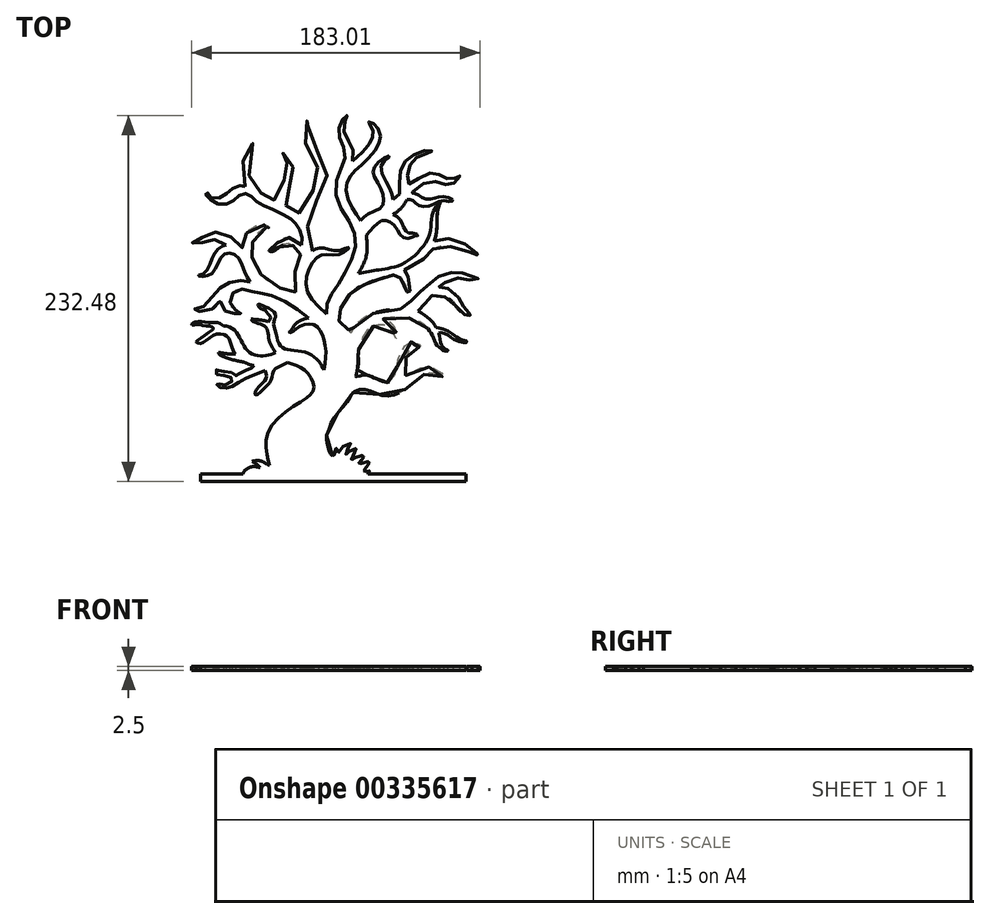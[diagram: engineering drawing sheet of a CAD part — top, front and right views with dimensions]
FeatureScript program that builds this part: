
annotation { "Feature Type Name" : "Feature", "Feature Type Description" : "" }
export const myFeature = defineFeature(function(context is Context, id is Id, definition is map)
    precondition{}
    {
        {
            var Q0;
            Q0=qCreatedBy(makeId("Top.planeOp"),FACE);
            var sketch = newSketch(context, id + "F0", { "sketchPlane" : qUnion([Q0])});
            skFitSpline(sketch, "E0", {"points": [v(-37.23, -92.22) * mm, v(-37.93, -89.5) * mm, v(-37.64, -70.07) * mm, v(-14, -49.38) * mm, v(-9.05, -42.86) * mm, v(-12.92, -33.47) * mm, v(-20.4, -28.62) * mm, v(-30.52, -26.33) * mm, v(-44.65, -28.9) * mm, v(-53.5, -26.46) * mm], "startDerivative": vector(-6.46, 28.02) * mm, "endDerivative": vector(-86.12, 39.68) * mm});
            skFitSpline(sketch, "E1", {"points": [v(-53.5, -26.46) * mm, v(-62.24, -24.53) * mm, v(-69.12, -21.43) * mm, v(-69.55, -20.32) * mm], "startDerivative": vector(-17.56, 2.77) * mm, "endDerivative": vector(-0.49, 6.57) * mm});
            skFitSpline(sketch, "E2", {"points": [v(-69.55, -20.32) * mm, v(-63.18, -21.35) * mm, v(-58.8, -21.52) * mm], "startDerivative": vector(12.15, -2.3) * mm, "endDerivative": vector(9.28, -0.04) * mm});
            skFitSpline(sketch, "E3", {"points": [v(-58.8, -21.52) * mm, v(-61.03, -17.47) * mm, v(-63.61, -10.67) * mm, v(-71.93, -9.08) * mm, v(-80.86, -14.69) * mm, v(-83.78, -13.74) * mm, v(-82.12, -12.32) * mm, v(-68.6, -3.79) * mm, v(-58.2, -7.58) * mm, v(-51.73, -18.6) * mm, v(-42.1, -22.64) * mm, v(-33.23, -20.57) * mm], "startDerivative": vector(-32.51, 46.9) * mm, "endDerivative": vector(77.44, 28.59) * mm});
            skFitSpline(sketch, "E4", {"points": [v(-33.23, -20.57) * mm, v(-37.27, -13.17) * mm, v(-39.86, -4.05) * mm, v(-47.76, -0.64) * mm, v(-48.83, 0.83) * mm], "startDerivative": vector(-16.8, 23.88) * mm, "endDerivative": vector(0.64, 6.3) * mm});
            skFitSpline(sketch, "E5", {"points": [v(-48.83, 0.83) * mm, v(-35.48, -2.55) * mm, v(-31.57, -14.02) * mm, v(-26.34, -18.5) * mm, v(-14.47, -20.28) * mm, v(-5.83, -26.09) * mm, v(-2.67, -31.48) * mm], "startDerivative": vector(73.32, -8.54) * mm, "endDerivative": vector(18.96, -39.09) * mm});
            skFitSpline(sketch, "E6", {"points": [v(-2.67, -31.48) * mm, v(-1.43, -19.6) * mm, v(-3.36, -10.05) * mm, v(-7.1, -3.92) * mm, v(-12.97, -2.37) * mm, v(-19.74, -4.89) * mm, v(-22.7, -7.34) * mm, v(-24.45, -7.73) * mm, v(-24.64, -7.2) * mm, v(-23.41, -6.37) * mm, v(-21.54, -3.28) * mm, v(-17.68, 0) * mm, v(-12.52, 1.37) * mm], "startDerivative": vector(16.4, 90.94) * mm, "endDerivative": vector(60.2, 10.33) * mm});
            skFitSpline(sketch, "E7", {"points": [v(-12.52, 1.37) * mm, v(-24.06, 10) * mm, v(-38, 16.41) * mm, v(-45.65, 17.78) * mm, v(-49.75, 18.87) * mm, v(-57.81, 19.42) * mm, v(-62.18, 13.68) * mm, v(-60.95, 8.35) * mm, v(-56.05, 5.43) * mm, v(-55.53, 4.23) * mm, v(-58.2, 4.23) * mm, v(-64.66, 5.34) * mm, v(-68.36, 11.89) * mm, v(-68.7, 12.49) * mm, v(-69.22, 12.32) * mm, v(-70.43, 10) * mm, v(-78.6, 5.6) * mm, v(-84.97, 6.9) * mm, v(-84.8, 7.24) * mm, v(-79.3, 8.79) * mm, v(-71.63, 17.4) * mm, v(-65, 22.99) * mm, v(-55.7, 25.14) * mm, v(-49.5, 24.45) * mm], "startDerivative": vector(-156.26, 128.1) * mm, "endDerivative": vector(126.07, -24.69) * mm});
            skFitSpline(sketch, "E8", {"points": [v(-49.5, 24.45) * mm, v(-52.85, 30.29) * mm, v(-56.83, 39.4) * mm, v(-61.9, 42.67) * mm, v(-66.9, 41.22) * mm, v(-70.51, 35) * mm, v(-73.99, 29.64) * mm, v(-78.7, 28.05) * mm, v(-82.24, 28.19) * mm, v(-82.31, 28.62) * mm, v(-81.95, 28.7) * mm, v(-78.9, 29.64) * mm, v(-74.78, 36.15) * mm, v(-72.25, 42.38) * mm, v(-67.83, 46.86) * mm, v(-64.72, 47.95) * mm], "startDerivative": vector(-43.88, 65.41) * mm, "endDerivative": vector(53.78, 11.6) * mm});
            skFitSpline(sketch, "E9", {"points": [v(-64.72, 47.95) * mm, v(-68.7, 50.12) * mm, v(-73.4, 51.28) * mm, v(-78.33, 50.27) * mm, v(-80.5, 49.18) * mm, v(-85.35, 48.96) * mm, v(-86.07, 49.1) * mm, v(-85.78, 49.61) * mm, v(-82.89, 50.92) * mm, v(-78.62, 53.81) * mm, v(-72.9, 55.91) * mm, v(-65.52, 54.75) * mm, v(-59.37, 50.84) * mm, v(-54.73, 46.28) * mm, v(-54.3, 46.5) * mm, v(-52.49, 53.96) * mm, v(-44.31, 60.4) * mm, v(-37.43, 59.68) * mm, v(-37.65, 59.1) * mm, v(-38.8, 59.24) * mm, v(-46.4, 53.02) * mm, v(-48.65, 44.48) * mm, v(-47.93, 38.47) * mm, v(-42.28, 28.99) * mm, v(-29.9, 20.37) * mm, v(-20.79, 17.84) * mm, v(-20.71, 18.06) * mm, v(-21.3, 28.26) * mm, v(-18.04, 39.84) * mm, v(-17.75, 42.6) * mm, v(-19.77, 45.63) * mm, v(-25.27, 48.67) * mm, v(-30.85, 46.65) * mm, v(-35.26, 43.75) * mm, v(-37.43, 44.19) * mm, v(-37.22, 44.55) * mm, v(-35.77, 45.34) * mm, v(-31.43, 50.34) * mm, v(-27.23, 52.58) * mm, v(-21.44, 51.71) * mm, v(-16.73, 47.95) * mm], "startDerivative": vector(-159.85, 95.28) * mm, "endDerivative": vector(153.51, -155.1) * mm});
            skFitSpline(sketch, "E10", {"points": [v(-16.73, 47.95) * mm, v(-16.73, 53.67) * mm, v(-19.41, 59.82) * mm, v(-21.8, 62.93) * mm, v(-27.3, 66.7) * mm, v(-38.3, 71.84) * mm, v(-45.4, 75.53) * mm, v(-48.58, 78.71) * mm, v(-52.78, 80.67) * mm, v(-57.48, 78.57) * mm, v(-61.97, 74.88) * mm, v(-68.63, 73.57) * mm, v(-75.36, 77.2) * mm, v(-77.68, 80.45) * mm, v(-76.66, 81.24) * mm, v(-76.45, 80.23) * mm, v(-72.76, 77.34) * mm, v(-65.37, 79.87) * mm, v(-60.52, 83.78) * mm, v(-54.95, 85.59) * mm, v(-52.63, 85.08) * mm], "startDerivative": vector(12.24, 106.84) * mm, "endDerivative": vector(59.66, -23.4) * mm});
            skFitSpline(sketch, "E11", {"points": [v(-52.63, 85.08) * mm, v(-54.59, 91.38) * mm, v(-53.72, 102.23) * mm, v(-50.25, 108.9) * mm, v(-47.86, 112) * mm, v(-47.86, 112.8) * mm, v(-47.5, 113.45) * mm, v(-46.63, 113.02) * mm, v(-46.77, 111.14) * mm, v(-47.93, 109.11) * mm, v(-50.25, 102.3) * mm, v(-50.17, 92.1) * mm, v(-47.06, 85.66) * mm, v(-42.72, 81.24) * mm, v(-41.78, 79.8) * mm, v(-35.77, 76.25) * mm, v(-34.32, 75.82) * mm, v(-34.25, 76.76) * mm, v(-31.79, 83.42) * mm, v(-28.17, 88.34) * mm, v(-25.27, 93.33) * mm, v(-25.2, 98.1) * mm, v(-27.23, 101.87) * mm, v(-29.11, 103.9) * mm, v(-29.62, 105.78) * mm, v(-29.26, 106.43) * mm, v(-28.53, 105.85) * mm, v(-28.82, 104.91) * mm, v(-26.72, 103.25) * mm, v(-22.16, 96.73) * mm, v(-21.94, 90) * mm, v(-24.7, 83.92) * mm, v(-27.37, 78.35) * mm, v(-27.37, 74.15) * mm, v(-26.65, 72.63) * mm, v(-22.81, 70.39) * mm, v(-18.76, 67.28) * mm, v(-18.69, 67.64) * mm, v(-12.97, 78.06) * mm, v(-9.93, 81.9) * mm, v(-6.38, 90) * mm, v(-6.31, 96.52) * mm, v(-11.09, 106) * mm, v(-14.63, 113.53) * mm, v(-15.5, 119.39) * mm, v(-13.4, 126.92) * mm, v(-11.81, 128.94) * mm, v(-11.23, 128.3) * mm, v(-11.74, 127.57) * mm, v(-12.82, 122) * mm, v(-10.44, 113.67) * mm, v(-5.3, 105.5) * mm, v(-1.03, 98.04) * mm, v(-1.53, 85.73) * mm, v(-5.95, 77.84) * mm, v(-12.32, 68.8) * mm, v(-12.82, 59.39) * mm, v(-10.87, 56.42) * mm, v(-9.93, 44.19) * mm], "startDerivative": vector(-120.08, 280.65) * mm, "endDerivative": vector(-5.28, -540.47) * mm});
            skFitSpline(sketch, "E12", {"points": [v(-9.93, 44.19) * mm, v(-7.69, 45.56) * mm, v(-3.85, 46.07) * mm, v(1.36, 44.9) * mm, v(7, 44.19) * mm, v(12.36, 46.21) * mm, v(13.3, 46.14) * mm, v(11.57, 44.19) * mm, v(5.7, 41.5) * mm, v(-2.26, 41.8) * mm, v(-7.18, 39.77) * mm, v(-12.68, 31.01) * mm, v(-13.26, 18.64) * mm, v(-1.03, 4.16) * mm], "startDerivative": vector(40.45, 30.37) * mm, "endDerivative": vector(114.16, -103.83) * mm});
            skFitSpline(sketch, "E13", {"points": [v(-1.03, 4.16) * mm, v(0, 12.2) * mm, v(5.27, 20.94) * mm, v(12.32, 33.52) * mm, v(17.54, 48.24) * mm, v(14.16, 61.43) * mm, v(5.88, 76.46) * mm, v(6.19, 92.1) * mm, v(10.8, 102.53) * mm, v(9.1, 112.04) * mm, v(6.65, 119.25) * mm, v(8.34, 126.15) * mm, v(10.94, 129.83) * mm, v(12.17, 129.99) * mm, v(10.8, 126.15) * mm, v(10.94, 117.72) * mm, v(15.24, 110.2) * mm, v(15.54, 101.3) * mm], "startDerivative": vector(2.52, 146.68) * mm, "endDerivative": vector(-17.17, -159.84) * mm});
            skFitSpline(sketch, "E14", {"points": [v(15.54, 101.3) * mm, v(20.45, 105.45) * mm, v(23.52, 108.67) * mm, v(27.05, 113.73) * mm, v(28.43, 120.94) * mm, v(25.97, 125.08) * mm, v(25.97, 126) * mm, v(29.8, 124.31) * mm, v(33.18, 117.1) * mm, v(29.96, 108.05) * mm, v(20, 97.62) * mm, v(13.86, 91.18) * mm, v(11.25, 83.36) * mm, v(15.54, 71.25) * mm, v(20.76, 63.27) * mm], "startDerivative": vector(77.02, 62.47) * mm, "endDerivative": vector(65.04, -83.73) * mm});
            skFitSpline(sketch, "E15", {"points": [v(20.76, 63.27) * mm, v(25.05, 67.26) * mm, v(33.95, 71.86) * mm, v(35.33, 76.61) * mm, v(33.34, 84.44) * mm, v(28.58, 93.33) * mm, v(31.19, 99.47) * mm, v(38.24, 104.37) * mm, v(39.01, 103.91) * mm, v(33.8, 98.85) * mm, v(38.86, 84.44) * mm, v(41.16, 76.61) * mm], "startDerivative": vector(41.17, 51.56) * mm, "endDerivative": vector(11.33, -71.84) * mm});
            skFitSpline(sketch, "E16", {"points": [v(41.16, 76.61) * mm, v(45.45, 80.6) * mm, v(45.29, 90.93) * mm, v(48.66, 100.29) * mm, v(54.18, 105.04) * mm, v(63.67, 108.12) * mm, v(65.97, 107.5) * mm, v(65.66, 107.04) * mm, v(59.09, 104.9) * mm, v(52.95, 99.98) * mm, v(50.5, 92.31) * mm, v(51.6, 86.62) * mm, v(60.83, 92.2) * mm, v(68.8, 93.27) * mm, v(74.16, 90.66) * mm, v(79.38, 89.9) * mm, v(83.36, 92.2) * mm, v(83.67, 91.89) * mm, v(79.68, 86.98) * mm, v(73.7, 86.37) * mm, v(64.96, 88.51) * mm, v(53.89, 81.83) * mm, v(50.2, 76.61) * mm, v(45.76, 70.63) * mm, v(41.16, 67.26) * mm], "startDerivative": vector(110.78, 80.65) * mm, "endDerivative": vector(-110.46, -69.26) * mm});
            skFitSpline(sketch, "E17", {"points": [v(41.16, 67.26) * mm, v(45.24, 64.63) * mm, v(47.07, 61.26) * mm, v(49.26, 57.16) * mm, v(51.45, 55.51) * mm, v(55.55, 55.33) * mm, v(57, 53.78) * mm, v(56.37, 53.6) * mm, v(55.28, 53.7) * mm, v(50.9, 52.05) * mm, v(46.89, 53.33) * mm, v(42.96, 59.07) * mm, v(38.4, 63.08) * mm, v(34.03, 63.27) * mm, v(28.92, 59.25) * mm, v(24.36, 54.06) * mm], "startDerivative": vector(63.37, -31.9) * mm, "endDerivative": vector(-49.93, -59.23) * mm});
            skFitSpline(sketch, "E18", {"points": [v(24.36, 54.06) * mm, v(24.36, 41.38) * mm, v(19.25, 29.8) * mm], "startDerivative": vector(2.56, -25.89) * mm, "endDerivative": vector(-12.77, -22.63) * mm});
            skFitSpline(sketch, "E19", {"points": [v(19.25, 29.8) * mm, v(27.1, 31.26) * mm, v(35.21, 32.53) * mm, v(48.07, 36.27) * mm, v(61.84, 49.13) * mm, v(65.3, 59.07) * mm, v(66.22, 67.19) * mm, v(70.78, 74.76) * mm, v(71.14, 74.76) * mm, v(69.96, 71.47) * mm, v(69.14, 61.17) * mm, v(68.68, 54.97) * mm, v(67.5, 50.32) * mm], "startDerivative": vector(92.84, 17.97) * mm, "endDerivative": vector(-20.5, -69.36) * mm});
            skFitSpline(sketch, "E20", {"points": [v(67.5, 50.32) * mm, v(73.24, 51.87) * mm, v(83.73, 50.32) * mm, v(89.93, 45.85) * mm, v(95.13, 42.66) * mm, v(96.22, 42.38) * mm, v(96.22, 41.65) * mm, v(94.76, 41.56) * mm, v(94.58, 40.92) * mm, v(93.21, 41.47) * mm, v(84.73, 45.4) * mm, v(71.05, 46.76) * mm, v(64.94, 44.02) * mm, v(60.66, 38.92) * mm, v(48.17, 31.66) * mm, v(47.97, 31.21) * mm, v(49.1, 30.12) * mm, v(51.78, 24.65) * mm, v(52.02, 18.07) * mm, v(51.94, 16.29) * mm, v(50.88, 16.45) * mm, v(49.18, 23.11) * mm, v(44.38, 27.82) * mm, v(42.27, 28.31) * mm, v(41.78, 28.72) * mm, v(39.35, 28.15) * mm, v(28.54, 24.98) * mm, v(21.96, 22.14) * mm, v(13.75, 16.53) * mm, v(8.47, 8.57) * mm, v(6.93, 3.45) * mm, v(7.25, -1.34) * mm, v(12.21, -5.16) * mm, v(14.4, -7.84) * mm, v(14.9, -7.36) * mm, v(22.37, 1.34) * mm, v(46.09, 7.27) * mm], "startDerivative": vector(168, 66.2) * mm, "endDerivative": vector(398.56, 17.42) * mm});
            skFitSpline(sketch, "E21", {"points": [v(46.09, 7.27) * mm, v(52.9, 12.63) * mm, v(59.47, 18.84) * mm, v(65.07, 23.59) * mm, v(69.81, 27.6) * mm, v(78.33, 30.4) * mm, v(84.54, 30.04) * mm, v(89.05, 29.07) * mm, v(92.58, 27.24) * mm, v(95.25, 26.75) * mm, v(94.65, 25.78) * mm, v(88.56, 26.02) * mm, v(82.1, 26.88) * mm, v(73.22, 23.59) * mm, v(70.79, 22.14) * mm, v(70.66, 21.03) * mm, v(75.05, 20.67) * mm, v(82.47, 14.95) * mm, v(85.64, 9.71) * mm, v(87.34, 6.91) * mm, v(90.26, 4.33) * mm, v(91.36, 4.33) * mm, v(90.38, 3.26) * mm, v(89.17, 2.65) * mm, v(87.34, 3.14) * mm, v(82.72, 6.91) * mm, v(76.26, 13.97) * mm, v(66.65, 15.92) * mm, v(64.94, 15.19) * mm, v(58.86, 7.27) * mm, v(57.15, 5.94) * mm], "startDerivative": vector(152.87, 113.18) * mm, "endDerivative": vector(-62.21, -32.26) * mm});
            skFitSpline(sketch, "E22", {"points": [v(57.15, 5.94) * mm, v(61.99, 2.85) * mm, v(67.5, -2.44) * mm, v(68.41, -4.26) * mm, v(71.56, -5.08) * mm, v(78.86, -8.46) * mm, v(84.92, -12.6) * mm, v(88.02, -13.15) * mm, v(88.02, -13.88) * mm, v(86.47, -14.2) * mm, v(79.81, -12.1) * mm, v(76.17, -9.41) * mm, v(71.74, -7.77) * mm, v(70.33, -8.1) * mm, v(70.33, -8.46) * mm, v(71.56, -14.02) * mm, v(73.34, -17.4) * mm, v(75.94, -18.94) * mm, v(76.08, -19.3) * mm, v(74.89, -19.63) * mm, v(72.56, -18.62) * mm, v(68.6, -14.93) * mm, v(66.32, -9.78) * mm, v(63.44, -5.31) * mm, v(59.66, -1.9) * mm, v(52.55, 1.2) * mm, v(39.76, 1.72) * mm, v(35.05, 1) * mm, v(39.45, -1.25) * mm, v(42.21, -4.94) * mm, v(43.75, -9.95) * mm, v(43.24, -11.59) * mm, v(42.72, -11.18) * mm, v(42.72, -10.26) * mm, v(37.5, -3.91) * mm, v(32.08, -2.89) * mm, v(25.32, -5.86) * mm, v(19.7, -17.12) * mm, v(19.18, -22.95) * mm, v(19.28, -27.56) * mm, v(17.65, -35.13) * mm, v(17.54, -35.75) * mm, v(23.38, -34.72) * mm, v(29.21, -36.57) * mm, v(35.87, -39.12) * mm, v(39.04, -39.02) * mm, v(43.34, -32.68) * mm, v(43.65, -30.22) * mm, v(47.33, -17.83) * mm, v(54.3, -13.43) * mm, v(57.62, -15.17) * mm, v(59.4, -16.4) * mm, v(57.62, -16.8) * mm, v(54.8, -16.3) * mm, v(50.5, -20.4) * mm, v(49.28, -28.48) * mm, v(49.38, -33.29) * mm, v(49.17, -34.93) * mm, v(50.7, -34.21) * mm, v(60.23, -29.8) * mm, v(70.67, -32.27) * mm, v(73.74, -35.75) * mm, v(72.61, -35.75) * mm, v(69.65, -34.1) * mm, v(63.1, -33.7) * mm, v(58.8, -35.64) * mm, v(51.63, -41.89) * mm, v(45.9, -45.78) * mm, v(35.35, -47.93) * mm, v(23.79, -43.83) * mm, v(15.5, -46.29) * mm, v(12.53, -51.2) * mm, v(3.72, -62.16) * mm, v(0, -70.45) * mm, v(-0.97, -74.78) * mm, v(1.22, -84.1) * mm, v(2.74, -86.23) * mm], "startDerivative": vector(316.06, -183.06) * mm, "endDerivative": vector(154.23, -155.5) * mm});
            skFitSpline(sketch, "E23", {"points": [v(-37.23, -92.22) * mm, v(-42.9, -89.27) * mm, v(-48.15, -89.53) * mm], "startDerivative": vector(-10.66, 5.99) * mm, "endDerivative": vector(-10.92, -1.79) * mm});
            skFitSpline(sketch, "E24", {"points": [v(-48.15, -89.53) * mm, v(-44.28, -92.2) * mm, v(-43.24, -93.49) * mm], "startDerivative": vector(7.24, -4.5) * mm, "endDerivative": vector(2.14, -3.32) * mm});
            skFitSpline(sketch, "E25", {"points": [v(-43.24, -93.49) * mm, v(-48.32, -93.02) * mm, v(-53.03, -95.51) * mm, v(-53.92, -97.56) * mm], "startDerivative": vector(-13.25, 3.2) * mm, "endDerivative": vector(-1.8, -8.27) * mm});
            skFitSpline(sketch, "E26", {"points": [v(-53.92, -97.56) * mm, v(-51.05, -96.88) * mm, v(-46.37, -97.56) * mm], "startDerivative": vector(6.09, 2.16) * mm, "endDerivative": vector(8.9, -2) * mm});
            skLineSegment(sketch, "E27", {"start": v(-46.37, -97.56) * mm, "end": v(-46.37, -97.56) * mm});
            skLineSegment(sketch, "E28", {"start": v(-84.8, 7.24) * mm, "end": v(-85.32, 24.31) * mm, "construction": true});
            skLineSegment(sketch, "E29", {"start": v(-85.32, 24.31) * mm, "end": v(91.36, 4.33) * mm, "construction": true});
            skFitSpline(sketch, "E30", {"points": [v(70.33, -8.1) * mm, v(68.72, -8.1) * mm, v(66.26, -7.43) * mm, v(63.44, -5.31) * mm], "startDerivative": vector(-5.7, -0.28) * mm, "endDerivative": vector(-6.95, 6.19) * mm});
            skFitSpline(sketch, "E31", {"points": [v(-34.41, -4.06) * mm, v(-34.29, 0) * mm, v(-33.2, 2.67) * mm, v(-35.78, 6.6) * mm, v(-41.56, 9.35) * mm, v(-44.25, 10.34) * mm, v(-44.5, 10) * mm, v(-43.16, 7.66) * mm, v(-39.92, 6.36) * mm, v(-38.47, 4.42) * mm, v(-36.48, 1.98) * mm, v(-37.97, -0.91) * mm], "startDerivative": vector(-4.06, 42.22) * mm, "endDerivative": vector(-27.8, -32.84) * mm});
            skFitSpline(sketch, "E32", {"points": [v(-66.39, -3.5) * mm, v(-69.47, -1.64) * mm, v(-75.72, -1.33) * mm, v(-83.78, -0.85) * mm, v(-86.63, -2.43) * mm, v(-86.16, -2.9) * mm, v(-82.76, -2.51) * mm, v(-79.75, -3.15) * mm, v(-73.11, -4.41) * mm, v(-73.18, -5.8) * mm], "startDerivative": vector(-25.1, 20.7) * mm, "endDerivative": vector(-9.63, -22.76) * mm});
            skFitSpline(sketch, "E33", {"points": [v(-28.41, -26.35) * mm, v(-37.58, -30.63) * mm, v(-44.34, -33.71) * mm, v(-52.48, -37.04) * mm, v(-60.53, -41.8) * mm, v(-66.41, -43.07) * mm, v(-70.63, -41.1) * mm, v(-69.94, -40.13) * mm, v(-67.5, -41.1) * mm, v(-60.83, -38.27) * mm, v(-63.57, -35.23) * mm, v(-71.2, -33.79) * mm, v(-70.33, -30.85) * mm, v(-69.25, -32.02) * mm, v(-61.9, -32.87) * mm, v(-58.08, -35.13) * mm, v(-54.83, -32.73) * mm, v(-48.07, -30.18) * mm, v(-46.87, -28.77) * mm], "startDerivative": vector(-105.13, -29.15) * mm, "endDerivative": vector(29.74, 40.47) * mm});
            skLineSegment(sketch, "E34", {"start": v(25.38, -97.56) * mm, "end": v(87.75, -97.56) * mm});
            skLineSegment(sketch, "E35", {"start": v(87.75, -97.56) * mm, "end": v(87.75, -102.35) * mm});
            skLineSegment(sketch, "E36", {"start": v(87.75, -102.35) * mm, "end": v(-81.07, -102.35) * mm});
            skLineSegment(sketch, "E37", {"start": v(-81.07, -102.35) * mm, "end": v(-81.07, -97.56) * mm});
            skLineSegment(sketch, "E38", {"start": v(-81.07, -97.56) * mm, "end": v(-46.37, -97.56) * mm});
            skFitSpline(sketch, "E39", {"points": [v(2.74, -86.23) * mm, v(3.57, -86.66) * mm, v(4.11, -84.1) * mm, v(5.53, -80.54) * mm, v(5.63, -81.32) * mm, v(6.37, -84.1) * mm, v(8.42, -81.08) * mm, v(14.45, -78.38) * mm, v(12.3, -81.57) * mm, v(11.41, -85.24) * mm, v(13.96, -82.74) * mm, v(18.08, -81.57) * mm, v(16.17, -84.8) * mm, v(14.85, -88.77) * mm, v(18.23, -86.23) * mm, v(23.08, -86.23) * mm, v(20.82, -88.53) * mm, v(19.45, -91.56) * mm, v(23.18, -90.04) * mm, v(26.7, -90.2) * mm, v(24.06, -93.08) * mm, v(22.74, -96.42) * mm, v(24.16, -95.63) * mm, v(26.17, -95.48) * mm, v(25.48, -96.8) * mm, v(25.38, -97.56) * mm], "startDerivative": vector(43.65, -35.45) * mm, "endDerivative": vector(4.37, -33.58) * mm});
            skFitSpline(sketch, "E40", {"points": [v(-25.76, -26.76) * mm, v(-31, -29.27) * mm, v(-34.93, -32.5) * mm, v(-35.97, -37.6) * mm, v(-39.9, -42.45) * mm, v(-45.8, -47.53) * mm, v(-45.91, -44.88) * mm, v(-40.83, -38.98) * mm, v(-39.2, -35.86) * mm, v(-39.98, -31.83) * mm], "startDerivative": vector(-45.07, -20.48) * mm, "endDerivative": vector(-15.86, 43.29) * mm});
            skFitSpline(sketch, "E41", {"points": [v(61.84, 49.13) * mm, v(65.02, 50.52) * mm, v(67.5, 50.32) * mm], "startDerivative": vector(6, 3.37) * mm, "endDerivative": vector(5.3, -1.12) * mm});
            skFitSpline(sketch, "E42", {"points": [v(19.25, 29.8) * mm, v(27.1, 31.26) * mm, v(35.21, 32.53) * mm, v(48.07, 36.27) * mm, v(61.84, 49.13) * mm, v(65.3, 59.07) * mm, v(66.22, 67.19) * mm, v(70.78, 74.76) * mm, v(71.14, 74.76) * mm, v(69.96, 71.47) * mm, v(69.14, 61.17) * mm, v(68.68, 54.97) * mm, v(67.5, 50.32) * mm], "startDerivative": vector(92.84, 17.97) * mm, "endDerivative": vector(-20.5, -69.36) * mm, "construction": true});
            skFitSpline(sketch, "E43", {"points": [v(50.2, 76.61) * mm, v(53.14, 76.61) * mm, v(56.3, 73.83) * mm, v(63.42, 72.53) * mm, v(72.48, 75.93) * mm, v(78.64, 75.61) * mm, v(79.12, 76.61) * mm, v(72.57, 78.6) * mm, v(67.14, 77.55) * mm, v(60.9, 77.4) * mm, v(56.05, 80.3) * mm, v(53.54, 80.95) * mm, v(53.89, 81.83) * mm], "startDerivative": vector(47.35, 9.13) * mm, "endDerivative": vector(27.39, 47.5) * mm});
            skSolve(sketch);
        }
        {
            var Q0;
            Q0=qSketchRegion(id+"F0",true);
            extrude(context, id + "F1", {"entities" : qUnion([Q0]), "depth" : 2.5 * mm});
        }
    });
